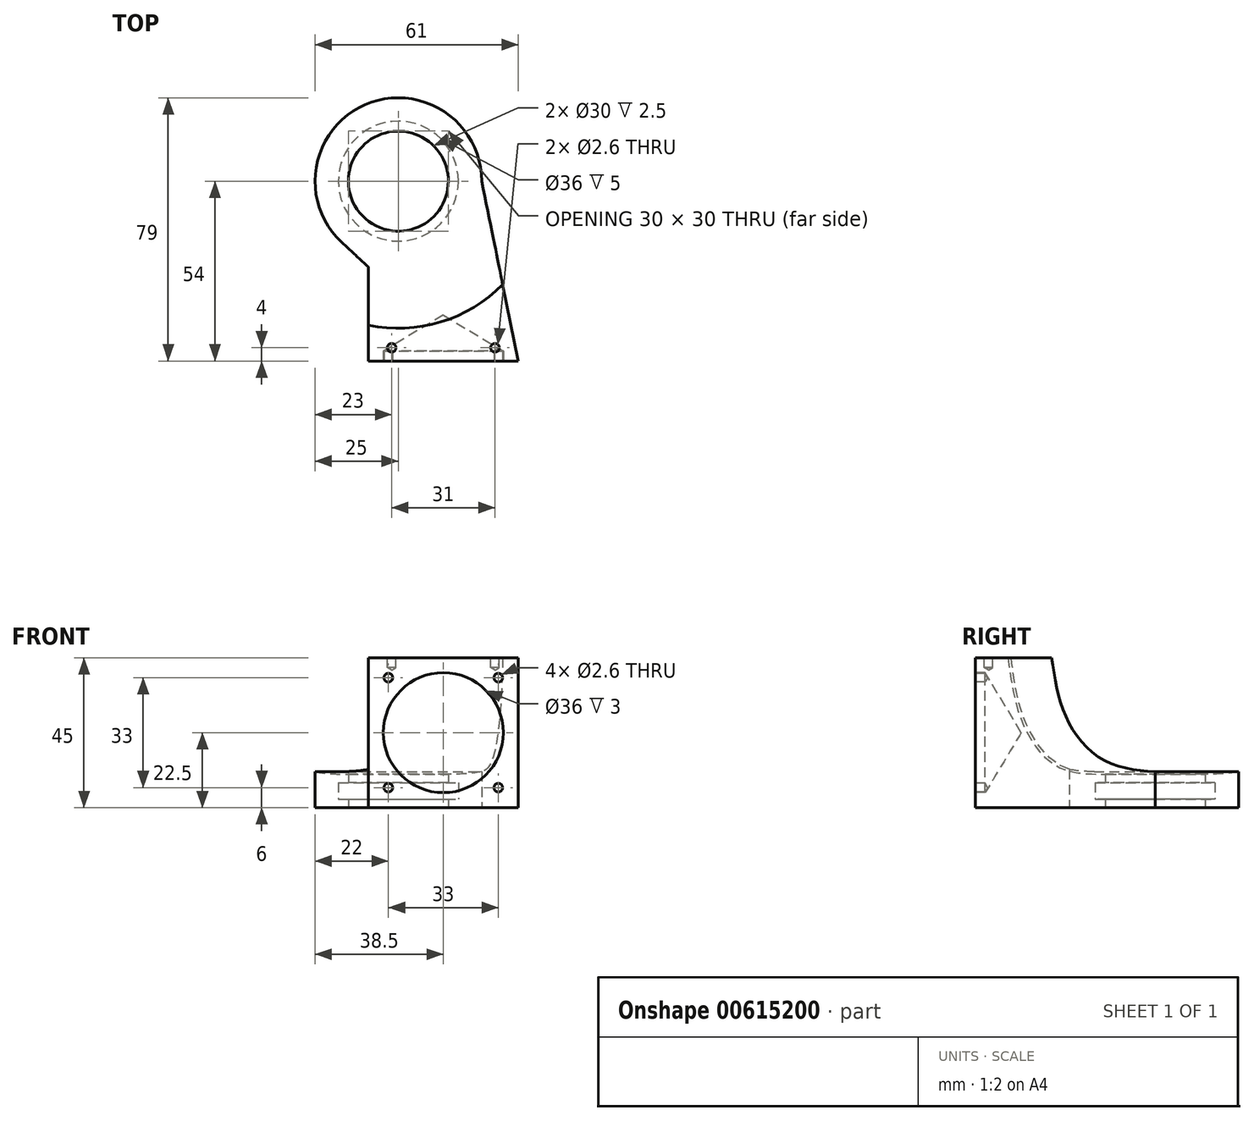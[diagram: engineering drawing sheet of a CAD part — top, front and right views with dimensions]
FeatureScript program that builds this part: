
annotation { "Feature Type Name" : "Feature", "Feature Type Description" : "" }
export const myFeature = defineFeature(function(context is Context, id is Id, definition is map)
    precondition{}
    {
        {
            var Q0;
            Q0=qCreatedBy(makeId("Top.planeOp"),FACE);
            var sketch = newSketch(context, id + "F0", { "sketchPlane" : qUnion([Q0])});
            skCircle(sketch, "E0", {"center": v(0, 0) * mm, "radius": 15 * mm});
            skLineSegment(sketch, "E1", {"start": v(0, 0) * mm, "end": v(0, -54) * mm});
            skLineSegment(sketch, "E2", {"start": v(0, -54) * mm, "end": v(-9, -54) * mm});
            skLineSegment(sketch, "E3", {"start": v(-9, -54) * mm, "end": v(-9, -25.77) * mm});
            skLineSegment(sketch, "E4", {"start": v(0, -54) * mm, "end": v(36, -54) * mm});
            skCircle(sketch, "E5", {"center": v(0, 0) * mm, "radius": 25 * mm});
            skLineSegment(sketch, "E6", {"start": v(-9, -25.77) * mm, "end": v(-17.02, -18.3) * mm});
            skLineSegment(sketch, "E7", {"start": v(25, 0) * mm, "end": v(36, -54) * mm});
            skSolve(sketch);
        }
        {
            var Q0;
            Q0 = qSketchRegion(id + "F0", true);
            extrude(context, id + "F1", {"entities" : qUnion([Q0]), "depth" : 45 * mm, "offsetDistance" : 25 * mm});
        }
        {
            var Q0;
            Q0=qCreatedBy(makeId("Right.planeOp"),FACE);
            var sketch = newSketch(context, id + "F2", { "sketchPlane" : qUnion([Q0])});
            skLineSegment(sketch, "E8", {"start": v(0, 0) * mm, "end": v(-15, 0) * mm});
            skLineSegment(sketch, "E9", {"start": v(-15, 0) * mm, "end": v(-15, 10) * mm});
            skLineSegment(sketch, "E10", {"start": v(-44.14, 45.06) * mm, "end": v(0, 45.06) * mm});
            skLineSegment(sketch, "E11", {"start": v(0, 45.06) * mm, "end": v(0, 0) * mm});
            skFitSpline(sketch, "E12", {"points": [v(-15, 10) * mm, v(-29.68, 12.58) * mm, v(-40.2, 26.36) * mm, v(-44.14, 45.06) * mm], "startDerivative": vector(-49.93, 0.63) * mm, "endDerivative": vector(-6.83, 53.96) * mm});
            skSolve(sketch);
        }
        {
            var Q0;
            Q0 = qSketchRegion(id + "F2", true);
            var Q1;
            Q1=sQuery(id+"F2.wireOp",EDGE,"E11");
            revolve(context, id + "F3", {"operationType" : NewBodyOperationType.REMOVE, "entities" : qUnion([Q0]), "axis" : qUnion([Q1]), "revolveType" : RevolveType.FULL, "oppositeDirection" : true});
        }
        {
            var Q0;
            Q0=makeQuery(id+"F1.opExtrude","CAP_FACE",FACE,{"disambiguationData":[OSD([sQuery(id+"F0.wireOp",EDGE,"E0"),sQuery(id+"F0.wireOp",EDGE,"E2"),sQuery(id+"F0.wireOp",EDGE,"E3"),sQuery(id+"F0.wireOp",EDGE,"E4"),sQuery(id+"F0.wireOp",EDGE,"E5"),sQuery(id+"F0.wireOp",EDGE,"E6"),sQuery(id+"F0.wireOp",EDGE,"E7")])],"isStart":false});
            var sketch = newSketch(context, id + "F4", { "sketchPlane" : qUnion([Q0])});
            skLineSegment(sketch, "E13", {"start": v(-9, -54) * mm, "end": v(-2, -54) * mm});
            skLineSegment(sketch, "E14", {"start": v(-2, -54) * mm, "end": v(-2, -50) * mm});
            skLineSegment(sketch, "E15", {"start": v(36, -54) * mm, "end": v(29, -54) * mm});
            skLineSegment(sketch, "E16", {"start": v(29, -54) * mm, "end": v(29, -50) * mm});
            skSolve(sketch);
        }
        {
            var Q0;
            Q0=sQuery(id+"F4.wireOp",VERTEX,"E14.end");
            var Q1;
            Q1=sQuery(id+"F4.wireOp",VERTEX,"E16.end");
            var Q2;
            Q2=makeQuery(id+"F1.opExtrude","SWEPT_BODY",BODY,{"disambiguationData":[OSD([sQuery(id+"F0.wireOp",EDGE,"E0"),sQuery(id+"F0.wireOp",EDGE,"E2"),sQuery(id+"F0.wireOp",EDGE,"E3"),sQuery(id+"F0.wireOp",EDGE,"E4"),sQuery(id+"F0.wireOp",EDGE,"E5"),sQuery(id+"F0.wireOp",EDGE,"E6"),sQuery(id+"F0.wireOp",EDGE,"E7")])]});
            hole(context, id + "F5", {"style" : HoleStyle.SIMPLE, "endStyle" : HoleEndStyle.BLIND, "holeDiameter" : 2.6 * mm, "majorDiameter" : 5 * mm, "holeDepth" : 3 * mm, "isTappedThrough" : true, "tappedDepth" : 12 * mm, "tapClearance" : 3, "locations" : qUnion([Q0, Q1]), "scope" : qUnion([Q2])});
        }
        {
            var Q0;
            Q0=makeQuery(id+"F1.opExtrude","SWEPT_FACE",FACE,{"disambiguationData":[OSD([sQuery(id+"F0.wireOp",EDGE,"E2"),sQuery(id+"F0.wireOp",EDGE,"E4")])]});
            var sketch = newSketch(context, id + "F6", { "sketchPlane" : qUnion([Q0])});
            skLineSegment(sketch, "E17", {"start": v(13.5, 0) * mm, "end": v(13.5, 22.5) * mm});
            skLineSegment(sketch, "E18", {"start": v(-9, 45) * mm, "end": v(-3, 45) * mm});
            skLineSegment(sketch, "E19", {"start": v(-3, 45) * mm, "end": v(-3, 39) * mm});
            skLineSegment(sketch, "E20", {"start": v(36, 45) * mm, "end": v(30, 45) * mm});
            skLineSegment(sketch, "E21", {"start": v(30, 45) * mm, "end": v(30, 39) * mm});
            skLineSegment(sketch, "E22", {"start": v(-9, 0) * mm, "end": v(-3, 0) * mm});
            skLineSegment(sketch, "E23", {"start": v(-3, 0) * mm, "end": v(-3, 6) * mm});
            skLineSegment(sketch, "E24", {"start": v(36, 0) * mm, "end": v(30, 0) * mm});
            skLineSegment(sketch, "E25", {"start": v(30, 0) * mm, "end": v(30, 6) * mm});
            skLineSegment(sketch, "E26", {"start": v(-3, 0) * mm, "end": v(13.5, 0) * mm});
            skSolve(sketch);
        }
        {
            var Q0;
            Q0=sQuery(id+"F6.wireOp",VERTEX,"E19.end");
            var Q1;
            Q1=sQuery(id+"F6.wireOp",VERTEX,"E21.end");
            var Q2;
            Q2=sQuery(id+"F6.wireOp",VERTEX,"E25.end");
            var Q3;
            Q3=sQuery(id+"F6.wireOp",VERTEX,"E23.end");
            var Q4;
            Q4=makeQuery(id+"F1.opExtrude","SWEPT_BODY",BODY,{"disambiguationData":[OSD([sQuery(id+"F0.wireOp",EDGE,"E0"),sQuery(id+"F0.wireOp",EDGE,"E2"),sQuery(id+"F0.wireOp",EDGE,"E3"),sQuery(id+"F0.wireOp",EDGE,"E4"),sQuery(id+"F0.wireOp",EDGE,"E5"),sQuery(id+"F0.wireOp",EDGE,"E6"),sQuery(id+"F0.wireOp",EDGE,"E7")])]});
            hole(context, id + "F7", {"style" : HoleStyle.SIMPLE, "endStyle" : HoleEndStyle.BLIND, "holeDiameter" : 2.6 * mm, "majorDiameter" : 5 * mm, "holeDepth" : 3 * mm, "isTappedThrough" : true, "tappedDepth" : 12 * mm, "tapClearance" : 3, "locations" : qUnion([Q0, Q1, Q2, Q3]), "scope" : qUnion([Q4])});
        }
        {
            var Q0;
            Q0=sQuery(id+"F6.wireOp",VERTEX,"E17.end");
            var Q1;
            Q1=makeQuery(id+"F1.opExtrude","SWEPT_BODY",BODY,{"disambiguationData":[OSD([sQuery(id+"F0.wireOp",EDGE,"E0"),sQuery(id+"F0.wireOp",EDGE,"E2"),sQuery(id+"F0.wireOp",EDGE,"E3"),sQuery(id+"F0.wireOp",EDGE,"E4"),sQuery(id+"F0.wireOp",EDGE,"E5"),sQuery(id+"F0.wireOp",EDGE,"E6"),sQuery(id+"F0.wireOp",EDGE,"E7")])]});
            hole(context, id + "F8", {"style" : HoleStyle.SIMPLE, "endStyle" : HoleEndStyle.BLIND, "holeDiameter" : 36 * mm, "majorDiameter" : 5 * mm, "holeDepth" : 3 * mm, "isTappedThrough" : true, "tappedDepth" : 12 * mm, "tapClearance" : 3, "locations" : qUnion([Q0]), "scope" : qUnion([Q1])});
        }
        {
            var Q0;
            Q0=qCreatedBy(makeId("Front.planeOp"),FACE);
            var sketch = newSketch(context, id + "F9", { "sketchPlane" : qUnion([Q0])});
            skLineSegment(sketch, "E27", {"start": v(0, 0) * mm, "end": v(0, 2.5) * mm});
            skLineSegment(sketch, "E28", {"start": v(0, 2.5) * mm, "end": v(18, 2.5) * mm});
            skLineSegment(sketch, "E29", {"start": v(18, 2.5) * mm, "end": v(18, 7.5) * mm});
            skLineSegment(sketch, "E30", {"start": v(18, 7.5) * mm, "end": v(8.02, 7.5) * mm});
            skLineSegment(sketch, "E31", {"start": v(8.02, 7.5) * mm, "end": v(0, 20.6) * mm});
            skLineSegment(sketch, "E32", {"start": v(0, 20.6) * mm, "end": v(0, 2.5) * mm});
            skSolve(sketch);
        }
        {
            var Q0;
            Q0 = qSketchRegion(id + "F9", true);
            var Q1;
            Q1=sQuery(id+"F9.wireOp",EDGE,"E32");
            revolve(context, id + "F10", {"operationType" : NewBodyOperationType.REMOVE, "entities" : qUnion([Q0]), "axis" : qUnion([Q1]), "revolveType" : RevolveType.FULL, "oppositeDirection" : true});
        }
    });
